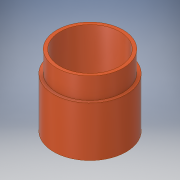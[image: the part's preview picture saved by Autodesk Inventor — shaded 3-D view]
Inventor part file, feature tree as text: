
AUTODESK INVENTOR PART (.ipt)
format: ipt  version: 2017 (Build 210142000, 142)  size: 156,672 bytes
history: native  units: in
note: dims shown in document units (in); Inventor stores cm internally (conversion verified against a paired STEP export)
features: revolve x1, sketch x1
ambient origin geometry x8: Origin, YZ Plane, XZ Plane, XY Plane, X Axis, Y Axis, Z Axis, Center Point
bodies: Solid1 (feature_tree)
feature tree (2):
  revolve  "Revolution1"  [1 undecoded]
  sketch  "Sketch1"  dims[d0=1.13in d1=3.7in d2=0.125in d3=0.1718in d5=1.0in d6=1.0in d7=90.0deg d8=0.5in d9=15.0deg d12=1.25in d13=0.25in d16=0.5in d17=0.5in d18=0.5in d19=2.5in d20=0.5in d22=0.375in d23=0.25in d25=0.234in d26=15.0deg d27=0.125in d28=0.25in d29=1.0in d30=4.25in d31=0.25in d32=1.0in d33=90.0deg]
note: 1 required parameter value undecoded (feature->parameter linkage not recoverable at this tier; creation-order binding heuristic only, values carry confidence <= 0.55)
